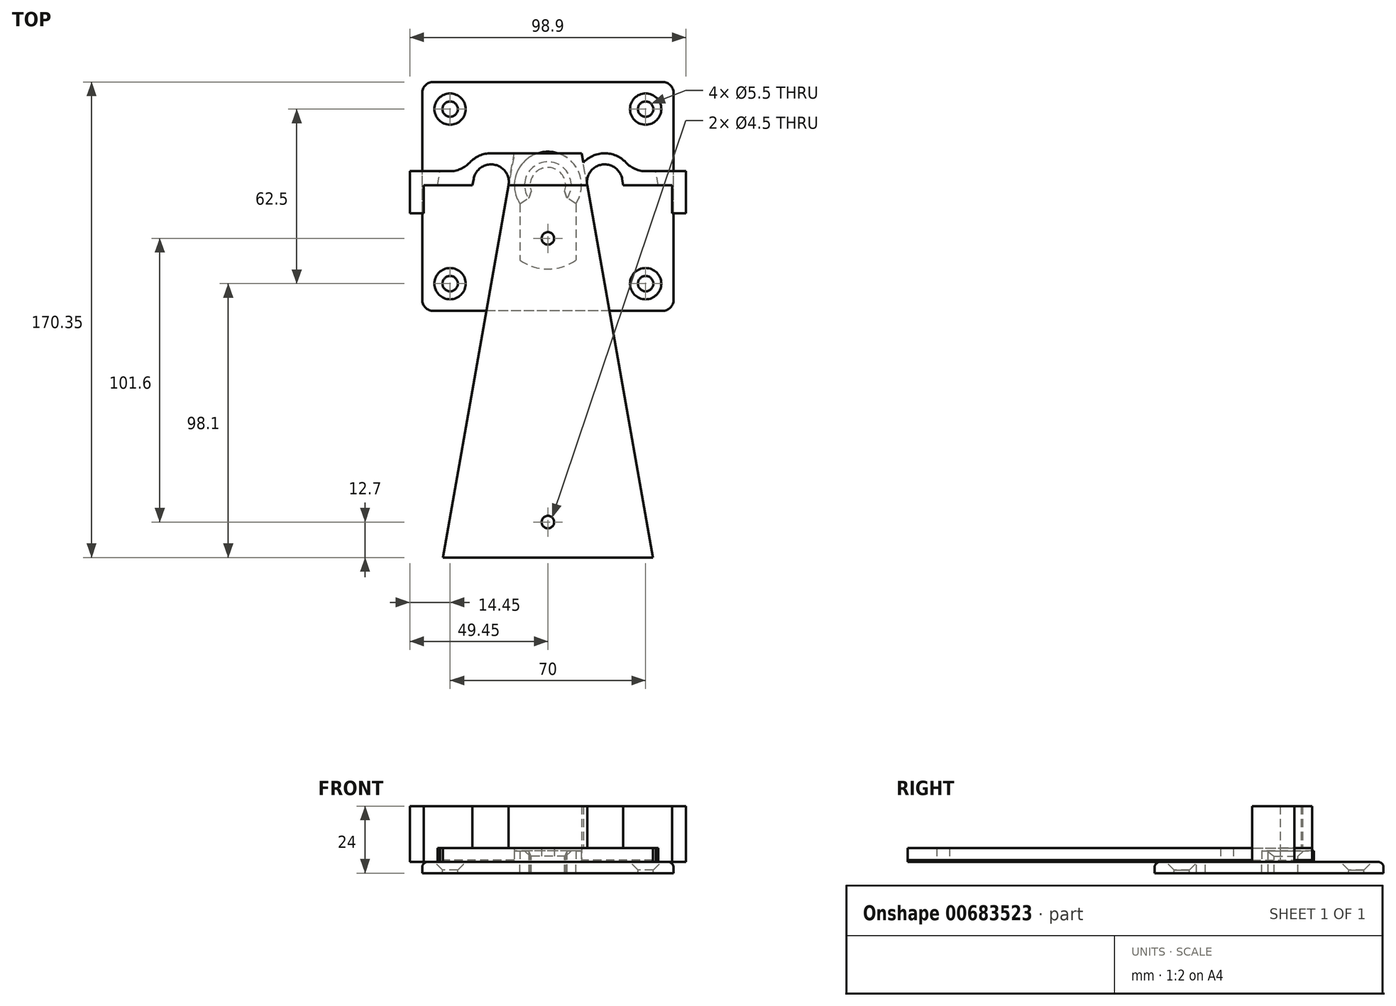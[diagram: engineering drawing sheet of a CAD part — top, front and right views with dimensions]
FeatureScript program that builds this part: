
annotation { "Feature Type Name" : "Feature", "Feature Type Description" : "" }
export const myFeature = defineFeature(function(context is Context, id is Id, definition is map)
    precondition{}
    {
        {
            var Q0;
            Q0=qCreatedBy(makeId("Top.planeOp"),FACE);
            var sketch = newSketch(context, id + "F0", { "sketchPlane" : qUnion([Q0])});
            skPoint(sketch, "E0.middle", {"position": v(0, 0) * mm});
            skCircle(sketch, "E1", {"center": v(0, 0) * mm, "radius": 6.35 * mm});
            skArc(sketch, "E2", {"start": v(10, -6.63) * mm, "mid": v(0, 12) * mm, "end": v(-10, -6.63) * mm});
            skLineSegment(sketch, "E3", {"start": v(-10, -6.63) * mm, "end": v(-10, -26.86) * mm});
            skLineSegment(sketch, "E4", {"start": v(10, -6.63) * mm, "end": v(10, -26.86) * mm});
            skLineSegment(sketch, "E5", {"start": v(-10, -6.63) * mm, "end": v(-5.3, -3.51) * mm});
            skLineSegment(sketch, "E6", {"start": v(10, -6.63) * mm, "end": v(5.3, -3.51) * mm});
            skArc(sketch, "E7", {"start": v(-10, -26.86) * mm, "mid": v(0, -30) * mm, "end": v(10, -26.86) * mm});
            skLineSegment(sketch, "E8.bottom", {"start": v(41, -45) * mm, "end": v(-41, -45) * mm});
            skLineSegment(sketch, "E8.top", {"start": v(41, 37) * mm, "end": v(-41, 37) * mm});
            skLineSegment(sketch, "E8.left", {"start": v(45, -41) * mm, "end": v(45, 33) * mm});
            skLineSegment(sketch, "E8.right", {"start": v(-45, -41) * mm, "end": v(-45, 33) * mm});
            skPoint(sketch, "E8.middle", {"position": v(0, -4) * mm});
            skLineSegment(sketch, "E9.bottom", {"start": v(35, -35.25) * mm, "end": v(-35, -35.25) * mm, "construction": true});
            skLineSegment(sketch, "E9.top", {"start": v(35, 27.25) * mm, "end": v(-35, 27.25) * mm, "construction": true});
            skLineSegment(sketch, "E9.left", {"start": v(35, -35.25) * mm, "end": v(35, 27.25) * mm, "construction": true});
            skLineSegment(sketch, "E9.right", {"start": v(-35, -35.25) * mm, "end": v(-35, 27.25) * mm, "construction": true});
            skPoint(sketch, "E10.visualSharp", {"position": v(-45, 37) * mm});
            skArc(sketch, "E10.filletArc", {"start": v(-41, 37) * mm, "mid": v(-43.83, 35.83) * mm, "end": v(-45, 33) * mm});
            skPoint(sketch, "E11.visualSharp", {"position": v(-45, -45) * mm});
            skArc(sketch, "E11.filletArc", {"start": v(-45, -41) * mm, "mid": v(-43.83, -43.83) * mm, "end": v(-41, -45) * mm});
            skPoint(sketch, "E12.visualSharp", {"position": v(45, -45) * mm});
            skArc(sketch, "E12.filletArc", {"start": v(41, -45) * mm, "mid": v(43.83, -43.83) * mm, "end": v(45, -41) * mm});
            skPoint(sketch, "E13.visualSharp", {"position": v(45, 37) * mm});
            skArc(sketch, "E13.filletArc", {"start": v(45, 33) * mm, "mid": v(43.83, 35.83) * mm, "end": v(41, 37) * mm});
            skSolve(sketch);
        }
        {
            var Q0;
            Q0=makeQuery(id+"F0.imprint","IMPRINT",FACE,{"disambiguationData":[TD([[makeQuery(id+"F0.imprint","IMPRINT",EDGE,{"derivedFrom":sQuery(id+"F0.wireOp",EDGE,"E0.bottom")}),1.0]])]});
            var Q1;
            Q1=makeQuery(id+"F0.imprint","IMPRINT",FACE,{"disambiguationData":[TD([[makeQuery(id+"F0.imprint","IMPRINT",EDGE,{"derivedFrom":sQuery(id+"F0.wireOp",EDGE,"E2")}),1.0]])]});
            var Q2;
            Q2=makeQuery(id+"F0.imprint","IMPRINT",FACE,{"disambiguationData":[TD([[makeQuery(id+"F0.imprint","IMPRINT",EDGE,{"derivedFrom":sQuery(id+"F0.wireOp",EDGE,"E2")}),-1.0]])]});
            extrude(context, id + "F1", {"entities" : qUnion([Q0, Q1, Q2]), "oppositeDirection" : true, "depth" : 4 * mm, "offsetDistance" : 25 * mm});
        }
        {
            var Q0;
            Q0=makeQuery(id+"F0.imprint","IMPRINT",FACE,{"disambiguationData":[TD([[makeQuery(id+"F0.imprint","IMPRINT",EDGE,{"derivedFrom":sQuery(id+"F0.wireOp",EDGE,"E2")}),1.0]])]});
            extrude(context, id + "F2", {"entities" : qUnion([Q0]), "operationType" : NewBodyOperationType.ADD, "depth" : 4 * mm, "offsetDistance" : 25 * mm});
        }
        {
            var Q0;
            Q0=makeQuery(id+"F2.opExtrude","CAP_EDGE",EDGE,{"disambiguationData":[OSD([sQuery(id+"F0.wireOp",EDGE,"E1")])],"isStart":false});
            var Q1;
            Q1=makeQuery(id+"F1.opExtrude","CAP_EDGE",EDGE,{"disambiguationData":[OSD([sQuery(id+"F0.wireOp",EDGE,"E0.bottom")])],"isStart":true});
            var Q2;
            {var subQ0=sQuery(id+"F0.wireOp",EDGE,"E5");var subQ1=sQuery(id+"F0.wireOp",EDGE,"E1");Q2=makeQuery(id+"F2.boolean.opBoolean","MERGE",EDGE,{"derivedFrom":[makeQuery(id+"F1.opExtrude","SWEPT_EDGE",EDGE,{"disambiguationData":[OSD([subQ1,subQ0])]}),makeQuery(id+"F2.opExtrude","SWEPT_EDGE",EDGE,{"disambiguationData":[OSD([subQ1,subQ0])]})]});}
            var Q3;
            {var subQ0=sQuery(id+"F0.wireOp",EDGE,"E6");var subQ1=sQuery(id+"F0.wireOp",EDGE,"E1");Q3=makeQuery(id+"F2.boolean.opBoolean","MERGE",EDGE,{"derivedFrom":[makeQuery(id+"F1.opExtrude","SWEPT_EDGE",EDGE,{"disambiguationData":[OSD([subQ1,subQ0])]}),makeQuery(id+"F2.opExtrude","SWEPT_EDGE",EDGE,{"disambiguationData":[OSD([subQ1,subQ0])]})]});}
            chamfer(context, id + "F3", {"entities" : qUnion([Q0, Q1, Q2, Q3]), "width" : 2 * mm, "tangentPropagation" : true});
        }
        {
            var Q0;
            Q0=sQuery(id+"F0.wireOp",VERTEX,"E9.top.end");
            var Q1;
            Q1=sQuery(id+"F0.wireOp",VERTEX,"E9.right.start");
            var Q2;
            Q2=sQuery(id+"F0.wireOp",VERTEX,"E9.bottom.start");
            var Q3;
            Q3=sQuery(id+"F0.wireOp",VERTEX,"E9.left.end");
            var Q4;
            Q4=makeQuery(id+"F1.opExtrude","SWEPT_BODY",BODY,{"disambiguationData":[OSD([sQuery(id+"F0.wireOp",EDGE,"E0.bottom"),sQuery(id+"F0.wireOp",EDGE,"E0.top"),sQuery(id+"F0.wireOp",EDGE,"E0.left"),sQuery(id+"F0.wireOp",EDGE,"E0.right"),sQuery(id+"F0.wireOp",EDGE,"f3c61182-643b-4fe4-a14f-2e32d98e132a.filletArc"),sQuery(id+"F0.wireOp",EDGE,"f990cf90-a4fe-4364-a49e-70ab754f6daf.filletArc"),sQuery(id+"F0.wireOp",EDGE,"761a327f-ef6f-47a1-9cf4-fbc57a3c436a.filletArc"),sQuery(id+"F0.wireOp",EDGE,"3ccf87df-6a84-43a0-bd4d-21ca41284786.filletArc"),sQuery(id+"F0.wireOp",EDGE,"E1"),sQuery(id+"F0.wireOp",EDGE,"3BwnxdNn-ZxHC-gA0N-O3Ev-xWau7Gdj6hs5"),sQuery(id+"F0.wireOp",EDGE,"E3"),sQuery(id+"F0.wireOp",EDGE,"E4"),sQuery(id+"F0.wireOp",EDGE,"E5"),sQuery(id+"F0.wireOp",EDGE,"E6")])]});
            hole(context, id + "F4", {"style" : HoleStyle.C_SINK, "endStyle" : HoleEndStyle.BLIND, "standardTappedOrClearance" : lookupTablePath({ "standard" : "ISO", "fit" : "Normal", "size" : "M5", "type" : "Clearance" }), "standardBlindInLast" : lookupTablePath({ "fit" : "Standard", "standard" : "ISO", "size" : "M5", "type" : "Clearance" }), "holeDiameter" : 5.5 * mm, "cSinkDiameter" : 11.2 * mm, "cSinkAngle" : 90 * degree, "majorDiameter" : 5 * mm, "holeDepth" : 8 * mm, "isTappedThrough" : true, "tappedDepth" : 12 * mm, "tapClearance" : 3, "locations" : qUnion([Q0, Q1, Q2, Q3]), "scope" : qUnion([Q4])});
        }
        {
            var Q0;
            Q0=makeQuery(id+"F1.opExtrude","CAP_EDGE",EDGE,{"disambiguationData":[OSD([sQuery(id+"F0.wireOp",EDGE,"E8.bottom")])],"isStart":true});
            fillet(context, id + "F5", {"entities" : qUnion([Q0]), "radius" : 2 * mm, "tangentPropagation" : true, "allowEdgeOverflow" : false});
        }
        {
            var Q0;
            Q0=qCreatedBy(makeId("Top.planeOp"),FACE);
            var sketch = newSketch(context, id + "F6", { "sketchPlane" : qUnion([Q0])});
            skLineSegment(sketch, "E14", {"start": v(-161.7, 0) * mm, "end": v(-26.27, 0) * mm, "construction": true});
            skLineSegment(sketch, "E15", {"start": v(-161.7, -139.7) * mm, "end": v(161.7, -139.7) * mm, "construction": true});
            skLineSegment(sketch, "E16", {"start": v(-44.45, 27.28) * mm, "end": v(-44.45, -172.79) * mm, "construction": true});
            skLineSegment(sketch, "E17", {"start": v(44.45, 27.28) * mm, "end": v(44.45, -172.79) * mm, "construction": true});
            skPoint(sketch, "E18", {"position": v(0, 0) * mm});
            skLineSegment(sketch, "E19", {"start": v(-44.45, 27.28) * mm, "end": v(44.45, 27.28) * mm, "construction": true});
            skPoint(sketch, "E20", {"position": v(0, 27.28) * mm});
            skLineSegment(sketch, "E21", {"start": v(-44.45, -139.7) * mm, "end": v(-19.82, 0) * mm});
            skLineSegment(sketch, "E22.0", {"start": v(-50.7, -138.6) * mm, "end": v(-26.07, 1.1) * mm, "construction": true});
            skLineSegment(sketch, "E23.0", {"start": v(-38.71, -139.7) * mm, "end": v(-14.08, 0) * mm});
            skLineSegment(sketch, "E24", {"start": v(-44.45, 0) * mm, "end": v(-44.45, -10) * mm});
            skLineSegment(sketch, "E25", {"start": v(-44.45, -10) * mm, "end": v(-49.45, -10) * mm});
            skLineSegment(sketch, "E26", {"start": v(-49.45, -10) * mm, "end": v(-49.45, 5) * mm});
            skLineSegment(sketch, "E27.MirrorCS", {"start": v(49.45, -10) * mm, "end": v(49.45, 5) * mm});
            skLineSegment(sketch, "E28.MirrorCS", {"start": v(44.45, -10) * mm, "end": v(49.45, -10) * mm});
            skLineSegment(sketch, "E29.MirrorCS", {"start": v(38.71, -139.7) * mm, "end": v(14.08, 0) * mm});
            skLineSegment(sketch, "E30", {"start": v(26.98, 0) * mm, "end": v(44.45, 0) * mm});
            skLineSegment(sketch, "E31", {"start": v(44.45, 0) * mm, "end": v(44.45, -10) * mm});
            skLineSegment(sketch, "E32", {"start": v(49.45, 5) * mm, "end": v(29.92, 5) * mm});
            skLineSegment(sketch, "E33", {"start": v(-38.71, -139.7) * mm, "end": v(38.71, -139.7) * mm});
            skLineSegment(sketch, "E34", {"start": v(-14.08, 0) * mm, "end": v(14.08, 0) * mm});
            skLineSegment(sketch, "E35.0", {"start": v(39.47, 0) * mm, "end": v(38.58, 5) * mm});
            skLineSegment(sketch, "E36.trimOffspring", {"start": v(-39.47, 0) * mm, "end": v(-38.58, 5) * mm});
            skPoint(sketch, "E37", {"position": v(0, -19.05) * mm});
            skPoint(sketch, "E38", {"position": v(0, -120.65) * mm});
            skLineSegment(sketch, "E39", {"start": v(-14.08, 0) * mm, "end": v(-30.53, 2.9) * mm, "construction": true});
            skArc(sketch, "E40", {"start": v(-14.08, 0) * mm, "mid": v(-19.23, 7.36) * mm, "end": v(-26.59, 2.2) * mm});
            skArc(sketch, "E41", {"start": v(-10.75, 5) * mm, "mid": v(-20.33, 11.45) * mm, "end": v(-29.92, 5) * mm});
            skArc(sketch, "E42.trimOffspring", {"start": v(-26.59, 0) * mm, "mid": v(-26.5, -0.39) * mm, "end": v(-26.4, -0.77) * mm});
            skLineSegment(sketch, "E43", {"start": v(-26.59, 2.2) * mm, "end": v(-26.98, 0) * mm});
            skArc(sketch, "E44.MirrorCS", {"start": v(10.75, 5) * mm, "mid": v(20.33, 11.45) * mm, "end": v(29.92, 5) * mm});
            skLineSegment(sketch, "E45.MirrorCS", {"start": v(26.59, 2.2) * mm, "end": v(26.98, 0) * mm});
            skArc(sketch, "E46.MirrorCS", {"start": v(14.08, 0) * mm, "mid": v(19.23, 7.36) * mm, "end": v(26.59, 2.2) * mm});
            skPoint(sketch, "E47.orphan", {"position": v(10.04, 0) * mm});
            skPoint(sketch, "E48.orphan", {"position": v(-10.04, 0) * mm});
            skLineSegment(sketch, "E49.trimOffspring", {"start": v(-29.92, 5) * mm, "end": v(-49.45, 5) * mm});
            skLineSegment(sketch, "E50.trimOffspring", {"start": v(10.75, 5) * mm, "end": v(-10.75, 5) * mm});
            skLineSegment(sketch, "E51.trimOffspring", {"start": v(26.98, 0) * mm, "end": v(161.7, 0) * mm, "construction": true});
            skLineSegment(sketch, "E52.trimOffspring", {"start": v(-14.08, 0) * mm, "end": v(14.08, 0) * mm, "construction": true});
            skLineSegment(sketch, "E53.trimOffspring", {"start": v(-26.27, 0) * mm, "end": v(-44.45, 0) * mm});
            skPoint(sketch, "E54.orphan", {"position": v(30.53, 2.9) * mm});
            skLineSegment(sketch, "E55", {"start": v(-20.33, 11.45) * mm, "end": v(20.33, 11.45) * mm});
            skLineSegment(sketch, "E56", {"start": v(14.08, 0) * mm, "end": v(12.06, 11.45) * mm});
            skLineSegment(sketch, "E57", {"start": v(-14.08, 0) * mm, "end": v(-12.06, 11.45) * mm});
            skLineSegment(sketch, "E58", {"start": v(-37.6, -133.35) * mm, "end": v(37.6, -133.35) * mm});
            skSolve(sketch);
        }
        {
            var Q0;
            {var subQ0=sQuery(id+"F6.wireOp",EDGE,"E34");Q0=makeQuery(id+"F6.imprint","IMPRINT",FACE,{"disambiguationData":[TD([[makeQuery(id+"F6.imprint","IMPRINT",EDGE,{"derivedFrom":subQ0}),-1.0]])]});}
            var Q1;
            {var subQ3=sQuery(id+"F6.wireOp",EDGE,"E27.MirrorCS");Q1=makeQuery(id+"F6.imprint","IMPRINT",FACE,{"disambiguationData":[TD([[makeQuery(id+"F6.imprint","IMPRINT",EDGE,{"derivedFrom":subQ3}),1.0]])]});}
            var Q2;
            {var subQ2=sQuery(id+"F6.wireOp",EDGE,"E24");Q2=makeQuery(id+"F6.imprint","IMPRINT",FACE,{"disambiguationData":[TD([[makeQuery(id+"F6.imprint","IMPRINT",EDGE,{"derivedFrom":subQ2}),-1.0]])]});}
            var Q3;
            {var subQ7=sQuery(id+"F6.wireOp",EDGE,"E34");Q3=makeQuery(id+"F6.imprint","IMPRINT",FACE,{"disambiguationData":[TD([[makeQuery(id+"F6.imprint","IMPRINT",EDGE,{"derivedFrom":subQ7}),1.0]])]});}
            var Q4;
            {var subQ0=sQuery(id+"F6.wireOp",EDGE,"E50.trimOffspring");Q4=makeQuery(id+"F6.imprint","IMPRINT",FACE,{"disambiguationData":[TD([[makeQuery(id+"F6.imprint","IMPRINT",EDGE,{"derivedFrom":subQ0}),-1.0]])]});}
            extrude(context, id + "F7", {"entities" : qUnion([Q0, Q1, Q2, Q3, Q4]), "depth" : 5 * mm, "offsetDistance" : 25 * mm});
        }
        {
            var Q0;
            {var subQ0=sQuery(id+"F6.wireOp",EDGE,"E32");var subQ1=sQuery(id+"F6.wireOp",EDGE,"E29.MirrorCS");var subQ2=makeQuery(id+"F6.imprint","INTERSECT",VERTEX,{"derivedFrom":[subQ1,subQ0]});Q0=makeQuery(id+"F6.imprint","IMPRINT",FACE,{"disambiguationData":[TD([[makeQuery(id+"F6.imprint","IMPRINT",EDGE,{"disambiguationData":[TD([[subQ2,1.0]])],"derivedFrom":subQ0}),1.0]])]});}
            var Q1;
            {var subQ0=sQuery(id+"F6.wireOp",EDGE,"0bce7d3b-4025-4c9f-b763-ae3607e670960.MirrorCS");Q1=makeQuery(id+"F6.imprint","IMPRINT",FACE,{"disambiguationData":[TD([[makeQuery(id+"F6.imprint","IMPRINT",EDGE,{"derivedFrom":subQ0}),-1.0]])]});}
            var Q2;
            {var subQ0=sQuery(id+"F6.wireOp",EDGE,"E44.MirrorCS");var subQ1=sQuery(id+"F6.wireOp",EDGE,"E32");var subQ2=makeQuery(id+"F6.imprint","INTERSECT",VERTEX,{"disambiguationData":[OD(0.0)],"derivedFrom":[subQ1,subQ0]});Q2=makeQuery(id+"F6.imprint","IMPRINT",FACE,{"disambiguationData":[TD([[makeQuery(id+"F6.imprint","IMPRINT",EDGE,{"disambiguationData":[TD([[subQ2,-1.0]])],"derivedFrom":subQ1}),-1.0]])]});}
            var Q3;
            {var subQ4=sQuery(id+"F6.wireOp",EDGE,"E35.0");Q3=makeQuery(id+"F6.imprint","IMPRINT",FACE,{"disambiguationData":[TD([[makeQuery(id+"F6.imprint","IMPRINT",EDGE,{"derivedFrom":subQ4}),1.0]])]});}
            var Q4;
            {var subQ3=sQuery(id+"F6.wireOp",EDGE,"E27.MirrorCS");Q4=makeQuery(id+"F6.imprint","IMPRINT",FACE,{"disambiguationData":[TD([[makeQuery(id+"F6.imprint","IMPRINT",EDGE,{"derivedFrom":subQ3}),1.0]])]});}
            var Q5;
            {var subQ0=sQuery(id+"F6.wireOp",EDGE,"E44.MirrorCS");var subQ1=sQuery(id+"F6.wireOp",EDGE,"E32");var subQ2=makeQuery(id+"F6.imprint","INTERSECT",VERTEX,{"disambiguationData":[OD(1.0)],"derivedFrom":[subQ1,subQ0]});Q5=makeQuery(id+"F6.imprint","IMPRINT",FACE,{"disambiguationData":[TD([[makeQuery(id+"F6.imprint","IMPRINT",EDGE,{"disambiguationData":[TD([[subQ2,-1.0]])],"derivedFrom":subQ1}),1.0]])]});}
            var Q6;
            {var subQ0=sQuery(id+"F6.wireOp",EDGE,"E32");var subQ1=sQuery(id+"F6.wireOp",EDGE,"E23.0");var subQ2=makeQuery(id+"F6.imprint","INTERSECT",VERTEX,{"derivedFrom":[subQ1,subQ0]});Q6=makeQuery(id+"F6.imprint","IMPRINT",FACE,{"disambiguationData":[TD([[makeQuery(id+"F6.imprint","IMPRINT",EDGE,{"disambiguationData":[TD([[subQ2,1.0]])],"derivedFrom":subQ0}),1.0]])]});}
            var Q7;
            {var subQ1=sQuery(id+"F6.wireOp",EDGE,"E32");var subQ6=makeQuery(id+"F6.imprint","INTERSECT",VERTEX,{"derivedFrom":[sQuery(id+"F6.wireOp",EDGE,"E23.0"),subQ1]});Q7=makeQuery(id+"F6.imprint","IMPRINT",FACE,{"disambiguationData":[TD([[makeQuery(id+"F6.imprint","IMPRINT",EDGE,{"disambiguationData":[TD([[subQ6,1.0]])],"derivedFrom":subQ1}),-1.0]])]});}
            var Q8;
            {var subQ0=sQuery(id+"F6.wireOp",EDGE,"E32");var subQ1=sQuery(id+"F6.wireOp",EDGE,"E23.0");var subQ2=makeQuery(id+"F6.imprint","INTERSECT",VERTEX,{"derivedFrom":[subQ1,subQ0]});Q8=makeQuery(id+"F6.imprint","IMPRINT",FACE,{"disambiguationData":[TD([[makeQuery(id+"F6.imprint","IMPRINT",EDGE,{"disambiguationData":[TD([[subQ2,-1.0]])],"derivedFrom":subQ0}),1.0]])]});}
            var Q9;
            {var subQ0=sQuery(id+"F6.wireOp",EDGE,"hRkIy495-XppM-99Ok-Q2qy-GYguamXwXfdJ");Q9=makeQuery(id+"F6.imprint","IMPRINT",FACE,{"disambiguationData":[TD([[makeQuery(id+"F6.imprint","IMPRINT",EDGE,{"derivedFrom":subQ0}),1.0]])]});}
            var Q10;
            {var subQ4=sQuery(id+"F6.wireOp",EDGE,"E36.trimOffspring");Q10=makeQuery(id+"F6.imprint","IMPRINT",FACE,{"disambiguationData":[TD([[makeQuery(id+"F6.imprint","IMPRINT",EDGE,{"derivedFrom":subQ4}),-1.0]])]});}
            var Q11;
            {var subQ3=sQuery(id+"F6.wireOp",EDGE,"E24");Q11=makeQuery(id+"F6.imprint","IMPRINT",FACE,{"disambiguationData":[TD([[makeQuery(id+"F6.imprint","IMPRINT",EDGE,{"derivedFrom":subQ3}),-1.0]])]});}
            var Q12;
            {var subQ0=sQuery(id+"F6.wireOp",EDGE,"E32");var subQ1=sQuery(id+"F6.wireOp",EDGE,"E29.MirrorCS");var subQ2=makeQuery(id+"F6.imprint","INTERSECT",VERTEX,{"derivedFrom":[subQ1,subQ0]});Q12=makeQuery(id+"F6.imprint","IMPRINT",FACE,{"disambiguationData":[TD([[makeQuery(id+"F6.imprint","IMPRINT",EDGE,{"disambiguationData":[TD([[subQ2,-1.0]])],"derivedFrom":subQ0}),1.0]])]});}
            var Q13;
            Q13=makeQuery(id+"F6.imprint","IMPRINT",FACE,{"disambiguationData":[TD([[makeQuery(id+"F6.imprint","IMPRINT",EDGE,{"derivedFrom":sQuery(id+"F6.wireOp",EDGE,"E34")}),1.0]])]});
            var Q14;
            {var subQ0=sQuery(id+"F6.wireOp",EDGE,"E50.trimOffspring");Q14=makeQuery(id+"F6.imprint","IMPRINT",FACE,{"disambiguationData":[TD([[makeQuery(id+"F6.imprint","IMPRINT",EDGE,{"derivedFrom":subQ0}),-1.0]])]});}
            var Q15;
            {var subQ0=sQuery(id+"F6.wireOp",EDGE,"E55");var subQ1=sQuery(id+"F6.wireOp",EDGE,"E44.MirrorCS");var subQ2=makeQuery(id+"F6.imprint","INTERSECT",VERTEX,{"derivedFrom":[subQ1,subQ0]});Q15=makeQuery(id+"F6.imprint","IMPRINT",FACE,{"disambiguationData":[TD([[makeQuery(id+"F6.imprint","IMPRINT",EDGE,{"disambiguationData":[TD([[subQ2,1.0]])],"derivedFrom":subQ1}),1.0]])]});}
            var Q16;
            {var subQ0=sQuery(id+"F6.wireOp",EDGE,"E55");var subQ1=sQuery(id+"F6.wireOp",EDGE,"E41");var subQ2=makeQuery(id+"F6.imprint","INTERSECT",VERTEX,{"derivedFrom":[subQ1,subQ0]});Q16=makeQuery(id+"F6.imprint","IMPRINT",FACE,{"disambiguationData":[TD([[makeQuery(id+"F6.imprint","IMPRINT",EDGE,{"disambiguationData":[TD([[subQ2,1.0]])],"derivedFrom":subQ1}),-1.0]])]});}
            extrude(context, id + "F8", {"entities" : qUnion([Q0, Q1, Q2, Q3, Q4, Q5, Q6, Q7, Q8, Q9, Q10, Q11, Q12, Q13, Q14, Q15, Q16]), "operationType" : NewBodyOperationType.ADD, "depth" : 20 * mm, "offsetDistance" : 25 * mm, "hasSecondDirection" : true, "secondDirectionOppositeDirection" : false, "secondDirectionDepth" : 5 * mm});
        }
        {
            var Q0;
            {var subQ5=sQuery(id+"F6.wireOp",EDGE,"E35.0");Q0=makeQuery(id+"F6.imprint","IMPRINT",FACE,{"disambiguationData":[TD([[makeQuery(id+"F6.imprint","IMPRINT",EDGE,{"derivedFrom":subQ5}),1.0]])]});}
            var Q1;
            {var subQ3=sQuery(id+"F6.wireOp",EDGE,"E36.trimOffspring");Q1=makeQuery(id+"F6.imprint","IMPRINT",FACE,{"disambiguationData":[TD([[makeQuery(id+"F6.imprint","IMPRINT",EDGE,{"derivedFrom":subQ3}),-1.0]])]});}
            extrude(context, id + "F9", {"entities" : qUnion([Q0, Q1]), "operationType" : NewBodyOperationType.REMOVE, "depth" : 5 * mm, "offsetDistance" : 25 * mm});
        }
        {
            var Q0;
            Q0=sQuery(id+"F6.wireOp",VERTEX,"E37");
            var Q1;
            Q1=sQuery(id+"F6.wireOp",VERTEX,"E38");
            var Q2;
            Q2=makeQuery(id+"F7.opExtrude","SWEPT_BODY",BODY,{"disambiguationData":[OSD([sQuery(id+"F6.wireOp",EDGE,"E23.0"),sQuery(id+"F6.wireOp",EDGE,"E29.MirrorCS"),sQuery(id+"F6.wireOp",EDGE,"E32"),sQuery(id+"F6.wireOp",EDGE,"E33")])]});
            hole(context, id + "F10", {"style" : HoleStyle.SIMPLE, "endStyle" : HoleEndStyle.BLIND, "oppositeDirection" : true, "standardTappedOrClearance" : lookupTablePath({ "standard" : "ANSI", "fit" : "Normal (ASME)", "size" : "#8", "type" : "Clearance" }), "standardBlindInLast" : lookupTablePath({ "fit" : "Free", "standard" : "ANSI", "size" : "#8", "type" : "Clearance" }), "holeDiameter" : 4.5 * mm, "majorDiameter" : 5 * mm, "holeDepth" : 8 * mm, "isTappedThrough" : true, "tappedDepth" : 12 * mm, "tapClearance" : 3, "locations" : qUnion([Q0, Q1]), "scope" : qUnion([Q2])});
        }
        {
            var Q0;
            {var subQ0=sQuery(id+"F6.wireOp",EDGE,"E23.0");Q0=makeQuery(id+"F9.boolean.opBoolean","MERGE",EDGE,{"derivedFrom":[makeQuery(id+"F7.opExtrude","CAP_EDGE",EDGE,{"disambiguationData":[OSD([subQ0])],"isStart":true}),makeQuery(id+"F9.opExtrude","CAP_EDGE",EDGE,{"disambiguationData":[OSD([subQ0])],"isStart":true})]});}
            var Q1;
            {var subQ0=sQuery(id+"F6.wireOp",EDGE,"E29.MirrorCS");Q1=makeQuery(id+"F9.boolean.opBoolean","MERGE",EDGE,{"derivedFrom":[makeQuery(id+"F7.opExtrude","CAP_EDGE",EDGE,{"disambiguationData":[OSD([subQ0])],"isStart":true}),makeQuery(id+"F9.opExtrude","CAP_EDGE",EDGE,{"disambiguationData":[OSD([subQ0])],"isStart":true})]});}
            chamfer(context, id + "F11", {"entities" : qUnion([Q0, Q1]), "chamferType" : ChamferType.TWO_OFFSETS, "width1" : .2 * mm, "oppositeDirection" : false, "width2" : .7 * mm, "tangentPropagation" : true});
        }
        {
            var Q0;
            Q0=makeQuery(id+"F8.opExtrude","SWEPT_EDGE",EDGE,{"disambiguationData":[OSD([sQuery(id+"F6.wireOp",EDGE,"E32"),sQuery(id+"F6.wireOp",EDGE,"E44.MirrorCS")])]});
            var Q1;
            Q1=makeQuery(id+"F8.opExtrude","SWEPT_EDGE",EDGE,{"disambiguationData":[OSD([sQuery(id+"F6.wireOp",EDGE,"E41"),sQuery(id+"F6.wireOp",EDGE,"E49.trimOffspring")])]});
            fillet(context, id + "F12", {"entities" : qUnion([Q0, Q1]), "radius" : 10 * mm, "tangentPropagation" : true, "allowEdgeOverflow" : false});
        }
    });
